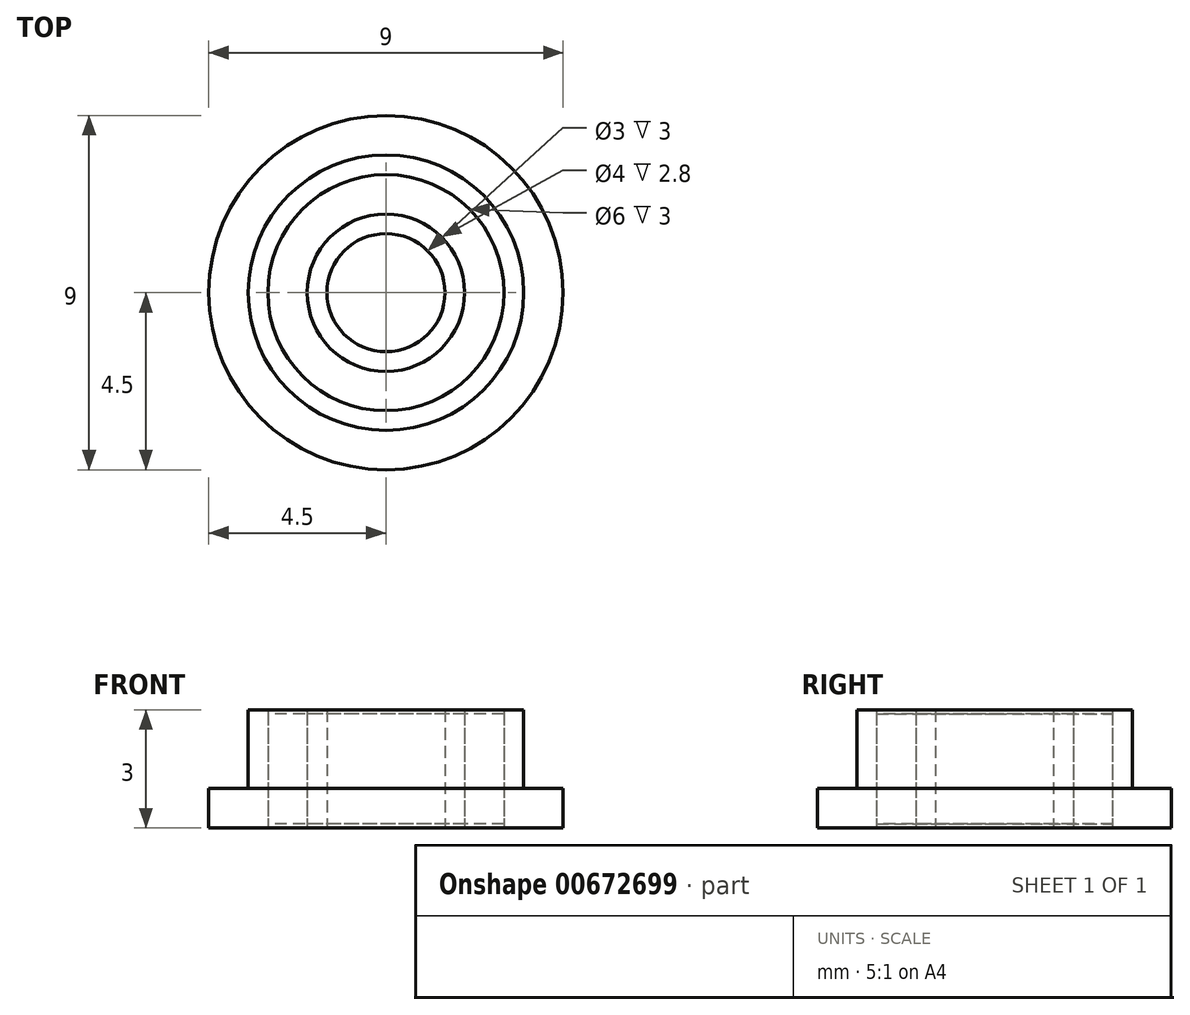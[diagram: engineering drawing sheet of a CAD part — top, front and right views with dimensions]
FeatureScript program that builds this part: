
annotation { "Feature Type Name" : "Feature", "Feature Type Description" : "" }
export const myFeature = defineFeature(function(context is Context, id is Id, definition is map)
    precondition{}
    {
        {
            var Q0;
            Q0=qCreatedBy(makeId("Top.planeOp"),FACE);
            var sketch = newSketch(context, id + "F0", { "sketchPlane" : qUnion([Q0])});
            skCircle(sketch, "E0", {"center": v(0, 0) * mm, "radius": 4.5 * mm});
            skCircle(sketch, "E1", {"center": v(0, 0) * mm, "radius": 3.5 * mm});
            skCircle(sketch, "E2", {"center": v(0, 0) * mm, "radius": 1.5 * mm});
            skCircle(sketch, "E3", {"center": v(0, 0) * mm, "radius": 3 * mm});
            skCircle(sketch, "E4", {"center": v(0, 0) * mm, "radius": 2 * mm});
            skSolve(sketch);
        }
        {
            var Q0;
            Q0 = qSketchRegion(id + "F0", true);
            extrude(context, id + "F1", {"entities" : qUnion([Q0]), "depth" : 1 * mm, "offsetDistance" : 25 * mm});
        }
        {
            var Q0;
            Q0=makeQuery(id+"F0.imprint","IMPRINT",FACE,{"disambiguationData":[TD([[makeQuery(id+"F0.imprint","IMPRINT",EDGE,{"derivedFrom":sQuery(id+"F0.wireOp",EDGE,"E2")}),-1.0]])]});
            var Q1;
            Q1=makeQuery(id+"F0.imprint","IMPRINT",FACE,{"disambiguationData":[TD([[makeQuery(id+"F0.imprint","IMPRINT",EDGE,{"derivedFrom":sQuery(id+"F0.wireOp",EDGE,"E1")}),1.0]])]});
            extrude(context, id + "F2", {"entities" : qUnion([Q0, Q1]), "operationType" : NewBodyOperationType.ADD, "depth" : 3 * mm, "offsetDistance" : 25 * mm});
        }
        {
            var Q0;
            Q0=makeQuery(id+"F0.imprint","IMPRINT",FACE,{"disambiguationData":[TD([[makeQuery(id+"F0.imprint","IMPRINT",EDGE,{"derivedFrom":sQuery(id+"F0.wireOp",EDGE,"E3")}),1.0]])]});
            extrude(context, id + "F3", {"entities" : qUnion([Q0]), "depth" : 2.9 * mm, "offsetDistance" : 25 * mm, "hasSecondDirection" : true, "secondDirectionOppositeDirection" : false, "secondDirectionDepth" : 0.1 * mm});
        }
    });
